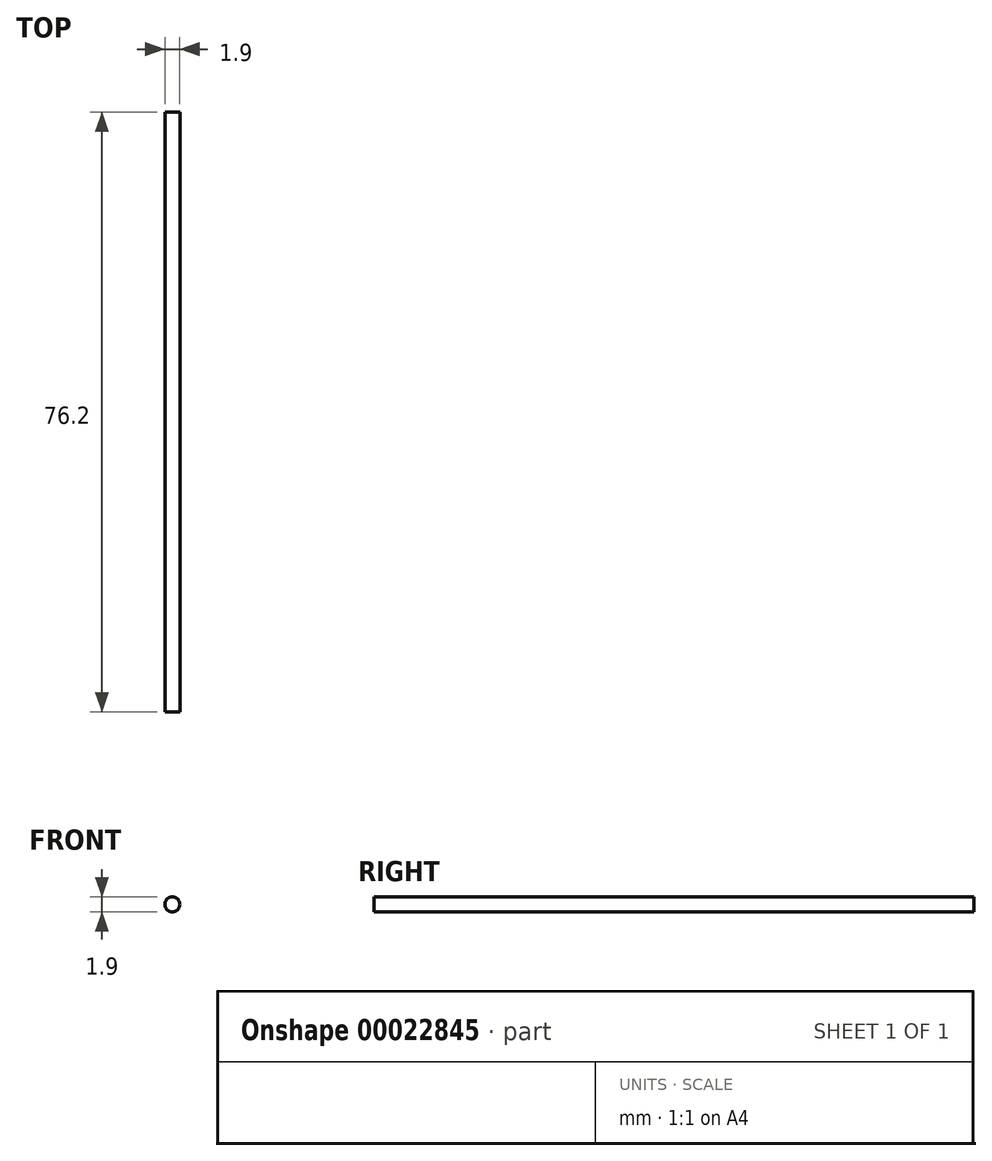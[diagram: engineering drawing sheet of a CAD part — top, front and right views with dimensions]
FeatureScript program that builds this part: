
annotation { "Feature Type Name" : "Feature", "Feature Type Description" : "" }
export const myFeature = defineFeature(function(context is Context, id is Id, definition is map)
    precondition{}
    {
        {
            var Q0;
            Q0=qCreatedBy(makeId("Front.planeOp"),FACE);
            var sketch = newSketch(context, id + "F0", { "sketchPlane" : qUnion([Q0])});
            skCircle(sketch, "E0", {"center": v(-86.12, 26.67) * mm, "radius": 0.95 * mm});
            skSolve(sketch);
        }
        {
            var Q0;
            Q0=makeQuery(id+"F0.imprint","IMPRINT",FACE,{"disambiguationData":[TD([[makeQuery(id+"F0.imprint","IMPRINT",EDGE,{"derivedFrom":sQuery(id+"F0.wireOp",EDGE,"E0")}),1.0]])]});
            extrude(context, id + "F1", {"entities" : qUnion([Q0]), "depth" : 76.2 * mm});
        }
    });
